# Revit family: 511_CP-UT_nailfin
name_source: partatom
category: Windows
revit_build: Autodesk Revit 2016 (Build: 20150220_1215(x64)
units: mm (PartAtom-declared; Revit-internal decimal feet)

## family parameters
Always vertical = Yes
Cut with Voids When Loaded = No
Host = Wall
OmniClass Number = 23.30.20.00
OmniClass Title = Windows
Room Calculation Point = No
Shared = No

## types (60) — shared parameters
Default Sill Height = 31 1/2"
MLW1 = 2 13/16"
MLW2 = 3 1/4"
Wall Closure = By host

## per-type parameters (varying)
| type | HBS | Height | MLH | MLW3 | MLW4 | VBS | Width |
| 36x48 | 18" | 48" | 15" | 2 1/4" | 2 1/4" | 18" | 36" |
| 72x84 | 30" | 84" | 27" | 3 3/4" | 4 1/2" | 36" | 72" |
| 96x96Max | 24" | 96" | 36" | 3" | 8 1/4" | 30" | 96" |
| 27x31.75Min | 12" | 31 3/4" | 9 7/8" | 1 1/2" | 1 11/16" | 13 1/2" | 27" |
| 48x48 | 18" | 48" | 15" | 2 1/4" | 3" | 24" | 48" |
| 60x60 | 18" | 60" | 21" | 2 1/4" | 3" | 36" | 60" |
| 84x84 | 18" | 84" | 33" | 2 1/4" | 6 3/4" | 30" | 84" |
| 30x36 | 12" | 36" | 12" | 1 1/2" | 1 1/2" | 18" | 30" |
| 30x42 | 12" | 42" | 15" | 1 1/2" | 1 1/2" | 18" | 30" |
| 30x48 | 18" | 48" | 15" | 2 1/4" | 1 1/2" | 18" | 30" |
| 30x54 | 18" | 54" | 18" | 2 1/4" | 1 1/2" | 18" | 30" |
| 36x36 | 12" | 36" | 12" | 1 1/2" | 2 1/4" | 18" | 36" |
| 36x42 | 12" | 42" | 15" | 1 1/2" | 2 1/4" | 18" | 36" |
| 36x54 | 18" | 54" | 18" | 2 1/4" | 2 1/4" | 18" | 36" |
| 36x60 | 18" | 60" | 21" | 2 1/4" | 2 1/4" | 18" | 36" |
| 42x36 | 12" | 36" | 12" | 1 1/2" | 2 1/4" | 24" | 42" |
| 42x42 | 12" | 42" | 15" | 1 1/2" | 2 1/4" | 24" | 42" |
| 42x48 | 12" | 48" | 18" | 1 1/2" | 2 1/4" | 24" | 42" |
| 42x54 | 18" | 54" | 18" | 2 1/4" | 2 1/4" | 24" | 42" |
| 42x60 | 18" | 60" | 21" | 2 1/4" | 2 1/4" | 24" | 42" |
| 42x66 | 18" | 66" | 24" | 2 1/4" | 2 1/4" | 24" | 42" |
| 42x72 | 18" | 72" | 27" | 2 1/4" | 2 1/4" | 24" | 42" |
| 48x42 | 12" | 42" | 15" | 1 1/2" | 3" | 24" | 48" |
| 48x54 | 18" | 54" | 18" | 2 1/4" | 3" | 24" | 48" |
| 48x60 | 18" | 60" | 21" | 2 1/4" | 3" | 24" | 48" |
| 48x66 | 18" | 66" | 24" | 2 1/4" | 3" | 24" | 48" |
| 48x72 | 18" | 72" | 27" | 2 1/4" | 3" | 24" | 48" |
| 48x78 | 18" | 78" | 30" | 2 1/4" | 3" | 24" | 48" |
| 54x48 | 12" | 48" | 18" | 1 1/2" | 3" | 30" | 54" |
| 54x54 | 18" | 54" | 18" | 2 1/4" | 3" | 30" | 54" |
| 54x60 | 18" | 60" | 21" | 2 1/4" | 3" | 30" | 54" |
| 54x66 | 18" | 66" | 24" | 2 1/4" | 3" | 30" | 54" |
| 54x72 | 18" | 72" | 27" | 2 1/4" | 3" | 30" | 54" |
| 54x78 | 18" | 78" | 30" | 2 1/4" | 3" | 30" | 54" |
| 54x84 | 18" | 84" | 33" | 2 1/4" | 3" | 30" | 54" |
| 54x90 | 18" | 90" | 36" | 2 1/4" | 3" | 30" | 54" |
| 60x54 | 12" | 54" | 21" | 1 1/2" | 3" | 36" | 60" |
| 60x66 | 18" | 66" | 24" | 2 1/4" | 3" | 36" | 60" |
| 60x72 | 18" | 72" | 27" | 2 1/4" | 3" | 36" | 60" |
| 60x78 | 18" | 78" | 30" | 2 1/4" | 3" | 36" | 60" |
| 60x84 | 18" | 84" | 33" | 2 1/4" | 3 3/4" | 30" | 60" |
| 60x90 | 18" | 90" | 36" | 2 1/4" | 3 3/4" | 30" | 60" |
| 60x96 | 24" | 96" | 36" | 3" | 3 3/4" | 30" | 60" |
| 66x60 | 12" | 60" | 24" | 1 1/2" | 3 3/4" | 36" | 66" |
| 66x66 | 18" | 66" | 24" | 2 1/4" | 3 3/4" | 36" | 66" |
| 66x72 | 18" | 72" | 27" | 2 1/4" | 3 3/4" | 36" | 66" |
| 66x78 | 18" | 78" | 30" | 2 1/4" | 3 3/4" | 36" | 66" |
| 66x84 | 18" | 84" | 33" | 2 1/4" | 4 1/2" | 30" | 66" |
| 66x90 | 18" | 90" | 36" | 2 1/4" | 4 1/2" | 30" | 66" |
| 66x96 | 24" | 96" | 36" | 3" | 4 1/2" | 30" | 66" |
| 84x78 | 18" | 78" | 30" | 2 1/4" | 6" | 36" | 84" |
| 84x90 | 18" | 90" | 36" | 2 1/4" | 6 3/4" | 30" | 84" |
| 84x96 | 24" | 96" | 36" | 3" | 6 3/4" | 30" | 84" |
| 90x78 | 18" | 78" | 30" | 2 1/4" | 6 3/4" | 36" | 90" |
| 90x84 | 18" | 84" | 33" | 2 1/4" | 7 1/2" | 30" | 90" |
| 90x90 | 18" | 90" | 36" | 2 1/4" | 7 1/2" | 30" | 90" |
| 90x96 | 24" | 96" | 36" | 3" | 7 1/2" | 30" | 90" |
| 96x78 | 18" | 78" | 30" | 2 1/4" | 7 1/2" | 36" | 96" |
| 96x84 | 18" | 84" | 33" | 2 1/4" | 8 1/4" | 30" | 96" |
| 96x90 | 18" | 90" | 36" | 2 1/4" | 8 1/4" | 30" | 96" |

## geometry (parser evidence)
native form markers: Sweep x2
no freeform markers — native parametric forms only
